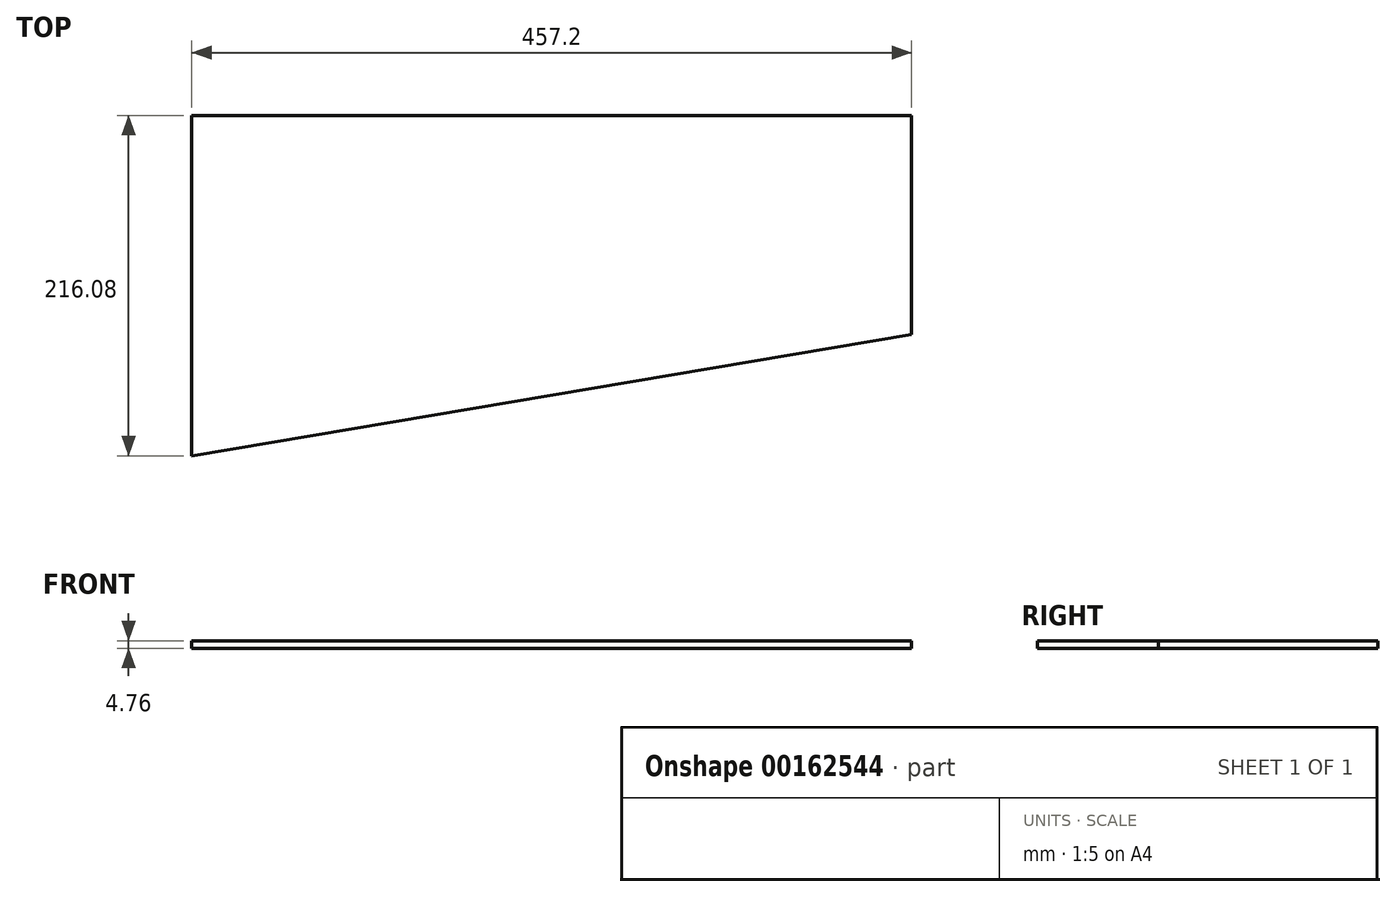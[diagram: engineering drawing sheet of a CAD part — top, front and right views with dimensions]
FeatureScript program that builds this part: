
annotation { "Feature Type Name" : "Feature", "Feature Type Description" : "" }
export const myFeature = defineFeature(function(context is Context, id is Id, definition is map)
    precondition{}
    {
        {
            var Q0;
            Q0=qCreatedBy(makeId("Top.planeOp"),FACE);
            var sketch = newSketch(context, id + "F0", { "sketchPlane" : qUnion([Q0])});
            skLineSegment(sketch, "E0.top", {"start": v(0, 225.33) * mm, "end": v(473.08, 225.33) * mm});
            skLineSegment(sketch, "E0.left", {"start": v(0, 9.25) * mm, "end": v(0, 225.33) * mm});
            skLineSegment(sketch, "E1", {"start": v(0, 9.25) * mm, "end": v(473.08, 88.8) * mm});
            skPoint(sketch, "E2.orphan", {"position": v(0, 0) * mm});
            skLineSegment(sketch, "E3", {"start": v(0, 4.48) * mm, "end": v(0, 9.25) * mm});
            skLineSegment(sketch, "E4", {"start": v(457.2, 225.33) * mm, "end": v(457.2, 86.14) * mm});
            skSolve(sketch);
        }
        {
            var Q0;
            Q0=qSketchRegion(id+"F0",true);
            extrude(context, id + "F1", {"entities" : qUnion([Q0]), "depth" : 4.76 * mm});
        }
    });
